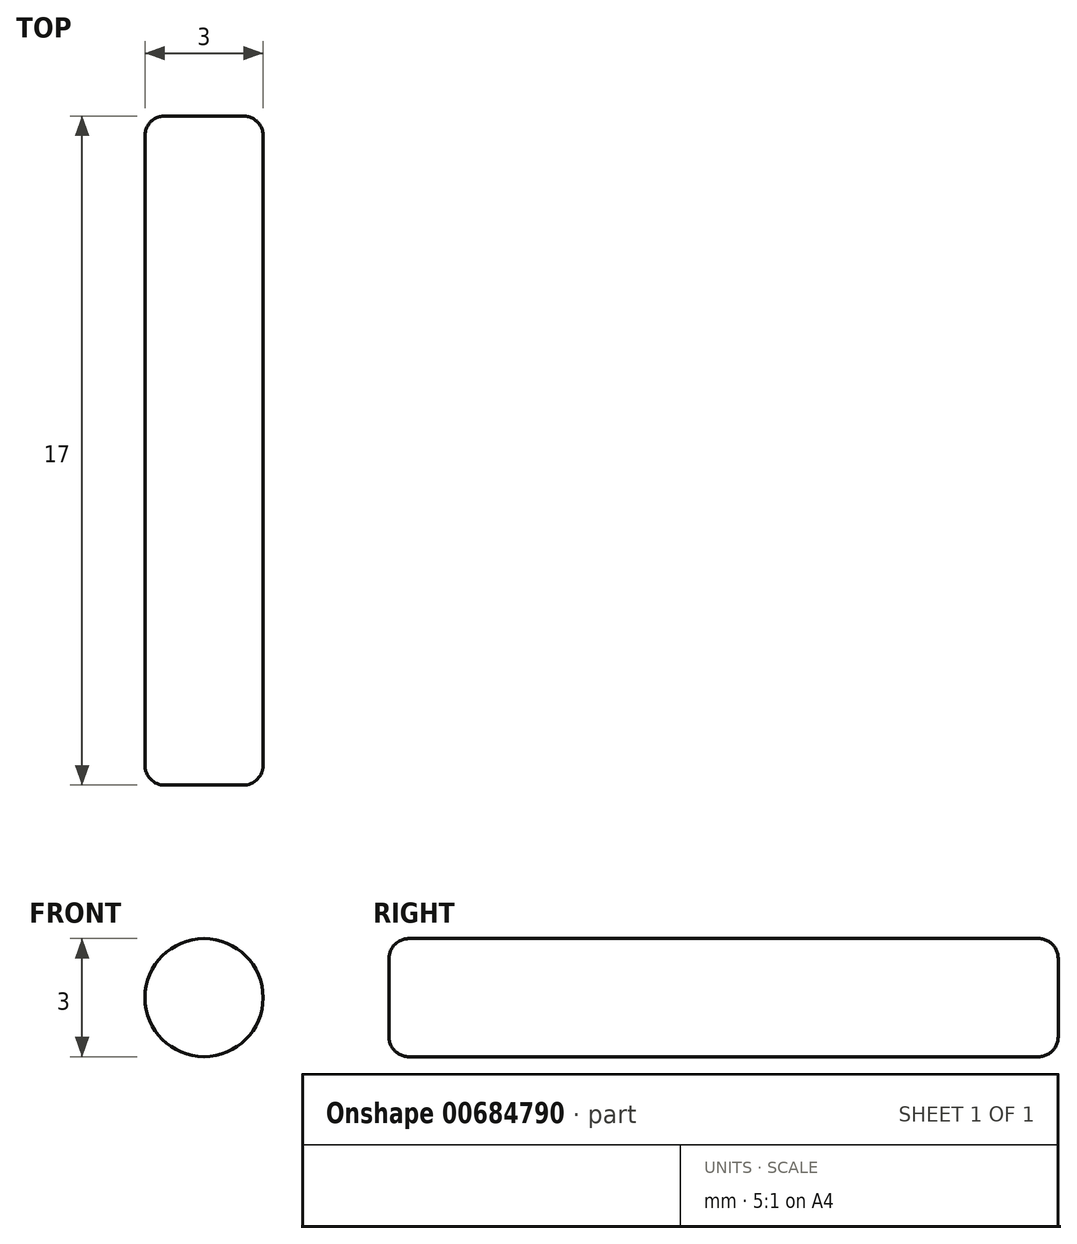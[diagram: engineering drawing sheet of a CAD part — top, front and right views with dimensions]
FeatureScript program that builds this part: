
annotation { "Feature Type Name" : "Feature", "Feature Type Description" : "" }
export const myFeature = defineFeature(function(context is Context, id is Id, definition is map)
    precondition{}
    {
        {
            var Q0;
            Q0=qCreatedBy(makeId("Front.planeOp"),FACE);
            var sketch = newSketch(context, id + "F0", { "sketchPlane" : qUnion([Q0])});
            skCircle(sketch, "E0", {"center": v(0, 0) * mm, "radius": 1.5 * mm});
            skSolve(sketch);
        }
        {
            var Q0;
            Q0=makeQuery(id+"F0.imprint","IMPRINT",FACE,{"disambiguationData":[TD([[makeQuery(id+"F0.imprint","IMPRINT",EDGE,{"derivedFrom":sQuery(id+"F0.wireOp",EDGE,"E0")}),1.0]])]});
            extrude(context, id + "F1", {"entities" : qUnion([Q0]), "depth" : 17 * mm, "offsetDistance" : 25 * mm});
        }
        {
            var Q0;
            Q0=makeQuery(id+"F1.opExtrude","SWEPT_FACE",FACE,{"disambiguationData":[OSD([sQuery(id+"F0.wireOp",EDGE,"E0")])]});
            var Q1;
            Q1=makeQuery(id+"F1.opExtrude","CAP_EDGE",EDGE,{"disambiguationData":[OSD([sQuery(id+"F0.wireOp",EDGE,"E0")])],"isStart":false});
            fillet(context, id + "F2", {"entities" : qUnion([Q0, Q1]), "radius" : .5 * mm, "tangentPropagation" : true, "allowEdgeOverflow" : false});
        }
    });
